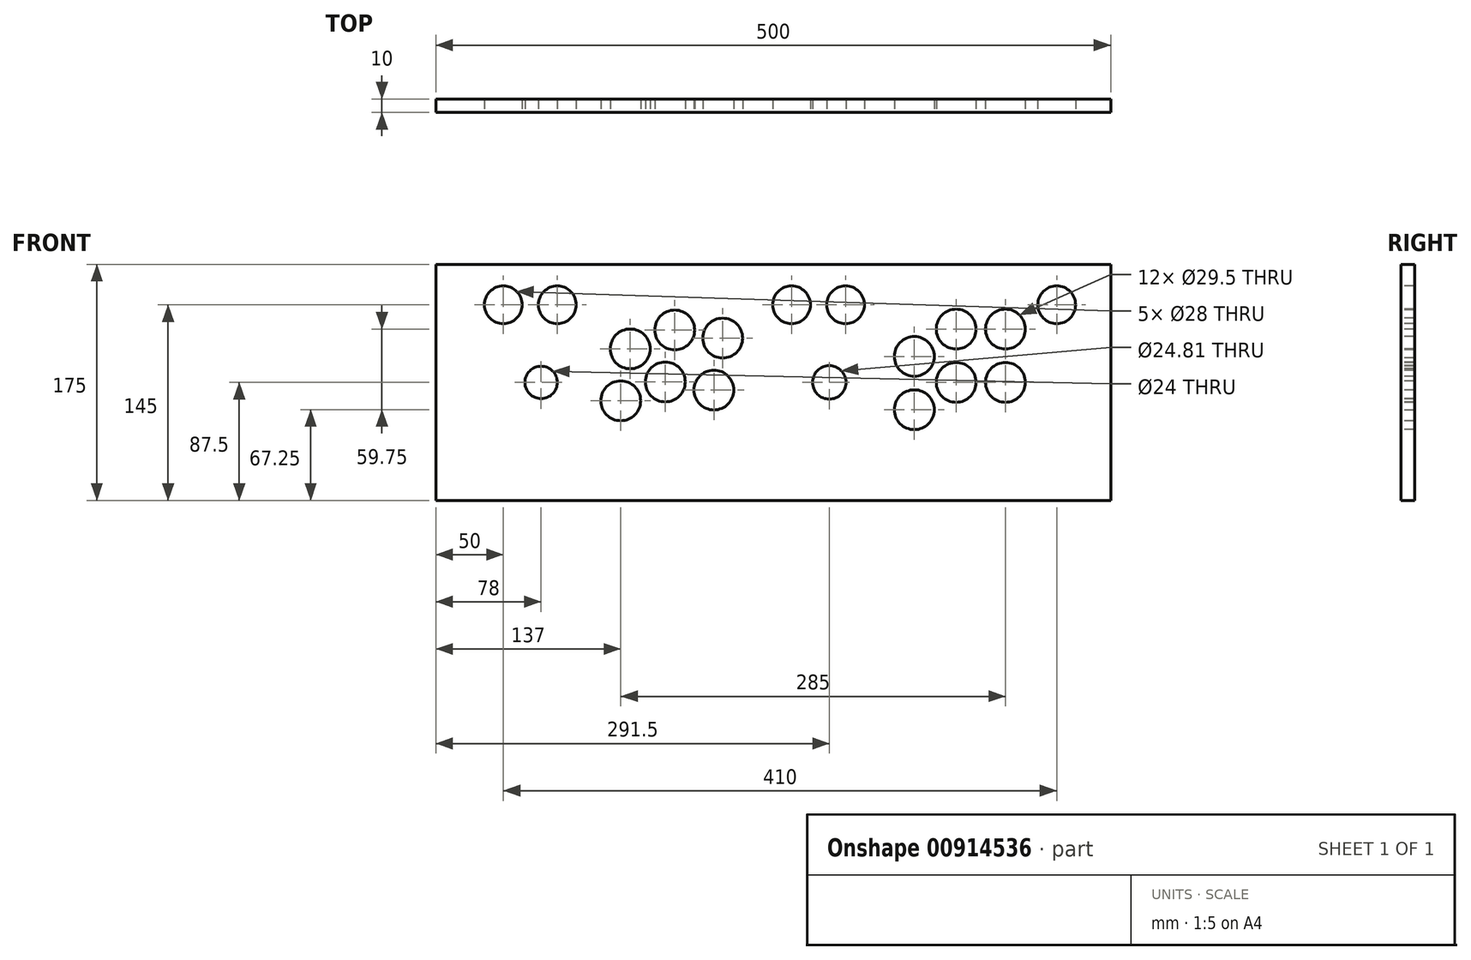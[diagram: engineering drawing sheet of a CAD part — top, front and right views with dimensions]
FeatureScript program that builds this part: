
annotation { "Feature Type Name" : "Feature", "Feature Type Description" : "" }
export const myFeature = defineFeature(function(context is Context, id is Id, definition is map)
    precondition{}
    {
        {
            var Q0;
            Q0=qCreatedBy(makeId("Front.planeOp"),FACE);
            var sketch = newSketch(context, id + "F0", { "sketchPlane" : qUnion([Q0])});
            skLineSegment(sketch, "E0.bottom", {"start": v(0, 0) * mm, "end": v(500, 0) * mm});
            skLineSegment(sketch, "E0.top", {"start": v(0, 175) * mm, "end": v(500, 175) * mm});
            skLineSegment(sketch, "E0.left", {"start": v(0, 0) * mm, "end": v(0, 175) * mm});
            skLineSegment(sketch, "E0.right", {"start": v(500, 0) * mm, "end": v(500, 175) * mm});
            skSolve(sketch);
        }
        {
            var Q0;
            Q0 = qSketchRegion(id + "F0", true);
            var Q1;
            Q1 = qSketchRegion(id + "F4", true);
            extrude(context, id + "F1", {"entities" : qUnion([Q0, Q1]), "depth" : 10 * mm, "offsetDistance" : 25 * mm});
        }
        {
            var Q0;
            Q0=makeQuery(id+"F1.opExtrude","CAP_FACE",FACE,{"disambiguationData":[OSD([sQuery(id+"F0.wireOp",EDGE,"E0.bottom"),sQuery(id+"F0.wireOp",EDGE,"E0.top"),sQuery(id+"F0.wireOp",EDGE,"E0.left"),sQuery(id+"F0.wireOp",EDGE,"E0.right")])],"isStart":false});
            var sketch = newSketch(context, id + "F2", { "sketchPlane" : qUnion([Q0])});
            skLineSegment(sketch, "E1", {"start": v(19.6, 30.97) * mm, "end": v(224.1, 30.97) * mm});
            skSolve(sketch);
        }
        {
            var Q0;
            Q0=makeQuery(id+"F2.imprint","IMPRINT",FACE,{"disambiguationData":[TD([[makeQuery(id+"F2.imprint","IMPRINT",EDGE,{"derivedFrom":makeQuery(id+"F1.opExtrude","CAP_EDGE",EDGE,{"disambiguationData":[OSD([sQuery(id+"F0.wireOp",EDGE,"E0.bottom")])],"isStart":false})}),1.0]])]});
            var sketch = newSketch(context, id + "F3", { "sketchPlane" : qUnion([Q0])});
            skCircle(sketch, "E2", {"center": v(177, 126.34) * mm, "radius": 14.75 * mm});
            skCircle(sketch, "E3", {"center": v(212.5, 120.34) * mm, "radius": 14.75 * mm});
            skCircle(sketch, "E4", {"center": v(206, 81.84) * mm, "radius": 14.75 * mm});
            skCircle(sketch, "E5", {"center": v(170, 87.84) * mm, "radius": 14.75 * mm});
            skCircle(sketch, "E6", {"center": v(137, 73.84) * mm, "radius": 14.75 * mm});
            skCircle(sketch, "E7", {"center": v(144, 112.34) * mm, "radius": 14.75 * mm});
            skCircle(sketch, "E8", {"center": v(78, 87.5) * mm, "radius": 12 * mm});
            skSolve(sketch);
        }
        {
            var Q0;
            Q0=makeQuery(id+"F1.opExtrude","CAP_FACE",FACE,{"disambiguationData":[OSD([sQuery(id+"F0.wireOp",EDGE,"E0.bottom"),sQuery(id+"F0.wireOp",EDGE,"E0.top"),sQuery(id+"F0.wireOp",EDGE,"E0.left"),sQuery(id+"F0.wireOp",EDGE,"E0.right")])],"isStart":false});
            var sketch = newSketch(context, id + "F4", { "sketchPlane" : qUnion([Q0])});
            skLineSegment(sketch, "E9", {"start": v(258.96, 30.87) * mm, "end": v(457.96, 30.87) * mm});
            skSolve(sketch);
        }
        {
            var Q0;
            Q0=makeQuery(id+"F1.opExtrude","CAP_FACE",FACE,{"disambiguationData":[OSD([sQuery(id+"F0.wireOp",EDGE,"E0.bottom"),sQuery(id+"F0.wireOp",EDGE,"E0.top"),sQuery(id+"F0.wireOp",EDGE,"E0.left"),sQuery(id+"F0.wireOp",EDGE,"E0.right")])],"isStart":false});
            var sketch = newSketch(context, id + "F5", { "sketchPlane" : qUnion([Q0])});
            skCircle(sketch, "E10", {"center": v(354.5, 106.75) * mm, "radius": 14.75 * mm});
            skCircle(sketch, "E11", {"center": v(385.5, 127) * mm, "radius": 14.75 * mm});
            skCircle(sketch, "E12", {"center": v(422, 127) * mm, "radius": 14.75 * mm});
            skCircle(sketch, "E13", {"center": v(422, 87.5) * mm, "radius": 14.75 * mm});
            skCircle(sketch, "E14", {"center": v(385.5, 87.5) * mm, "radius": 14.75 * mm});
            skCircle(sketch, "E15", {"center": v(354.5, 67.25) * mm, "radius": 14.75 * mm});
            skCircle(sketch, "E16", {"center": v(291.5, 87.5) * mm, "radius": 12.4 * mm});
            skSolve(sketch);
        }
        {
            var Q0;
            Q0=makeQuery(id+"F3.imprint","IMPRINT",FACE,{"disambiguationData":[TD([[makeQuery(id+"F3.imprint","IMPRINT",EDGE,{"derivedFrom":sQuery(id+"F3.wireOp",EDGE,"E2")}),-1.0]])]});
            var sketch = newSketch(context, id + "F6", { "sketchPlane" : qUnion([Q0])});
            skCircle(sketch, "E17", {"center": v(263.5, 145) * mm, "radius": 14 * mm});
            skCircle(sketch, "E18", {"center": v(50, 145) * mm, "radius": 14 * mm});
            skCircle(sketch, "E19", {"center": v(90, 145) * mm, "radius": 14 * mm});
            skCircle(sketch, "E20", {"center": v(303.5, 145) * mm, "radius": 14 * mm});
            skCircle(sketch, "E21", {"center": v(460, 145) * mm, "radius": 14 * mm});
            skSolve(sketch);
        }
        {
            var Q0;
            Q0=makeQuery(id+"F5.imprint","IMPRINT",FACE,{"disambiguationData":[TD([[makeQuery(id+"F5.imprint","IMPRINT",EDGE,{"derivedFrom":sQuery(id+"F5.wireOp",EDGE,"E10")}),1.0]])]});
            var Q1;
            Q1=makeQuery(id+"F5.imprint","IMPRINT",FACE,{"disambiguationData":[TD([[makeQuery(id+"F5.imprint","IMPRINT",EDGE,{"derivedFrom":sQuery(id+"F5.wireOp",EDGE,"E11")}),1.0]])]});
            var Q2;
            Q2=makeQuery(id+"F5.imprint","IMPRINT",FACE,{"disambiguationData":[TD([[makeQuery(id+"F5.imprint","IMPRINT",EDGE,{"derivedFrom":sQuery(id+"F5.wireOp",EDGE,"E12")}),1.0]])]});
            var Q3;
            Q3=makeQuery(id+"F5.imprint","IMPRINT",FACE,{"disambiguationData":[TD([[makeQuery(id+"F5.imprint","IMPRINT",EDGE,{"derivedFrom":sQuery(id+"F5.wireOp",EDGE,"E13")}),1.0]])]});
            var Q4;
            Q4=makeQuery(id+"F5.imprint","IMPRINT",FACE,{"disambiguationData":[TD([[makeQuery(id+"F5.imprint","IMPRINT",EDGE,{"derivedFrom":sQuery(id+"F5.wireOp",EDGE,"E14")}),1.0]])]});
            var Q5;
            Q5=makeQuery(id+"F5.imprint","IMPRINT",FACE,{"disambiguationData":[TD([[makeQuery(id+"F5.imprint","IMPRINT",EDGE,{"derivedFrom":sQuery(id+"F5.wireOp",EDGE,"E15")}),1.0]])]});
            var Q6;
            Q6=makeQuery(id+"F5.imprint","IMPRINT",FACE,{"disambiguationData":[TD([[makeQuery(id+"F5.imprint","IMPRINT",EDGE,{"derivedFrom":sQuery(id+"F5.wireOp",EDGE,"E16")}),1.0]])]});
            extrude(context, id + "F7", {"entities" : qUnion([Q0, Q1, Q2, Q3, Q4, Q5, Q6]), "operationType" : NewBodyOperationType.REMOVE, "oppositeDirection" : true, "depth" : 25 * mm, "offsetDistance" : 25 * mm});
        }
        {
            var Q0;
            Q0 = qSketchRegion(id + "F3", true);
            extrude(context, id + "F8", {"entities" : qUnion([Q0]), "operationType" : NewBodyOperationType.REMOVE, "oppositeDirection" : true, "depth" : 25 * mm, "offsetDistance" : 25 * mm});
        }
        {
            var Q0;
            Q0 = qSketchRegion(id + "F6", true);
            extrude(context, id + "F9", {"entities" : qUnion([Q0]), "operationType" : NewBodyOperationType.REMOVE, "oppositeDirection" : true, "depth" : 25 * mm, "offsetDistance" : 25 * mm});
        }
    });
